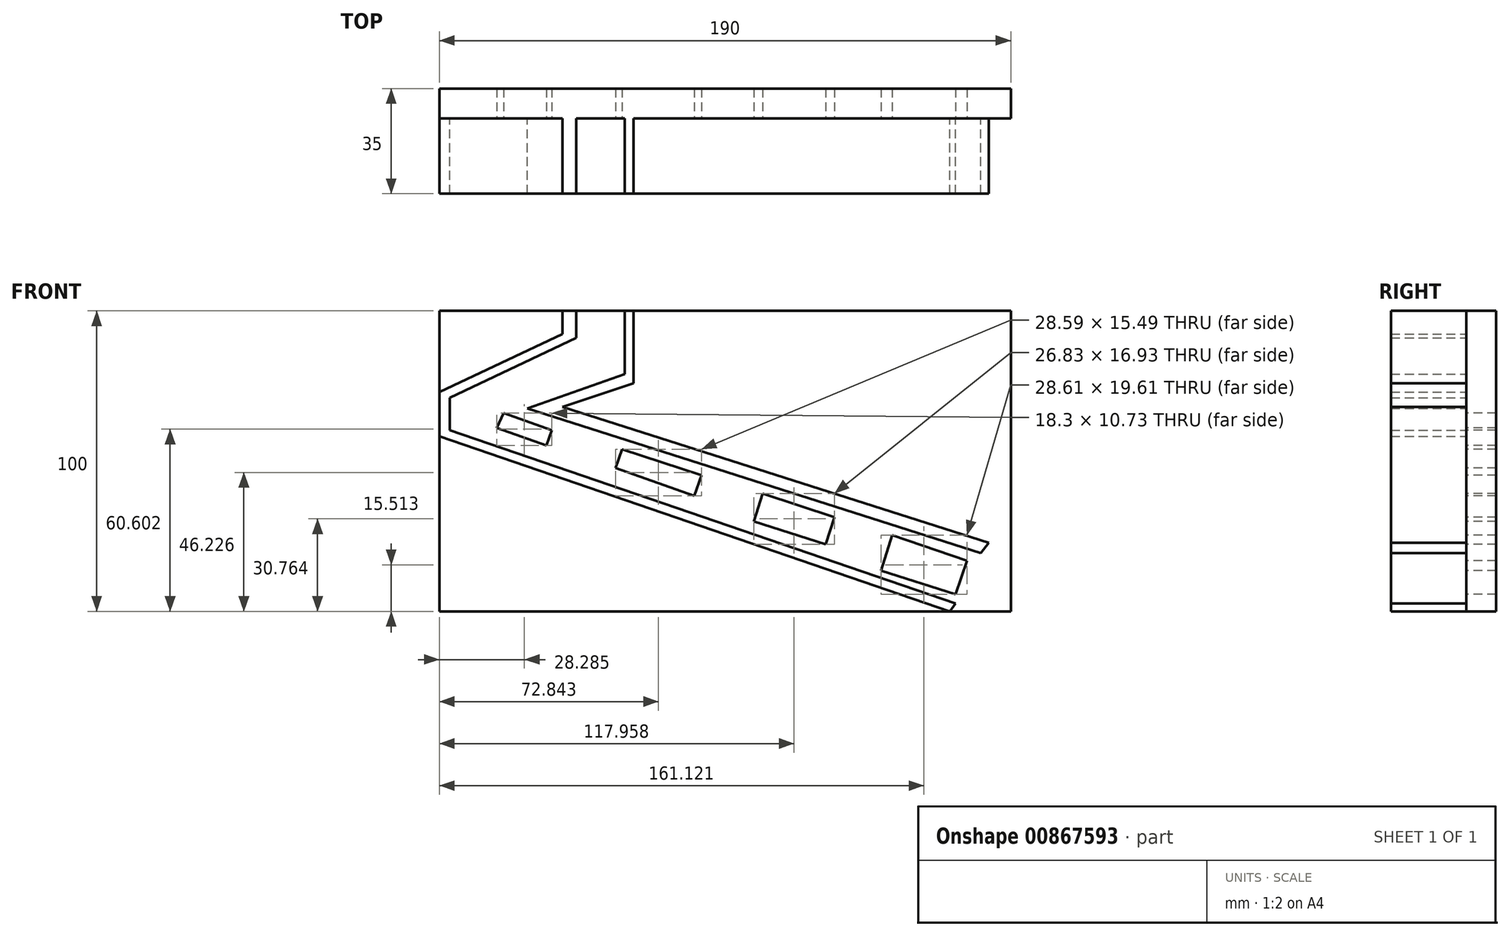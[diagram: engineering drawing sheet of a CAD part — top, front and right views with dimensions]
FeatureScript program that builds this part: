
annotation { "Feature Type Name" : "Feature", "Feature Type Description" : "" }
export const myFeature = defineFeature(function(context is Context, id is Id, definition is map)
    precondition{}
    {
        {
            var Q0;
            Q0=qCreatedBy(makeId("Front.planeOp"),FACE);
            var sketch = newSketch(context, id + "F0", { "sketchPlane" : qUnion([Q0])});
            skLineSegment(sketch, "E0.bottom", {"start": v(-95, 50) * mm, "end": v(95, 50) * mm});
            skLineSegment(sketch, "E0.top", {"start": v(-95, -50) * mm, "end": v(95, -50) * mm});
            skLineSegment(sketch, "E0.left", {"start": v(-95, 50) * mm, "end": v(-95, -50) * mm});
            skLineSegment(sketch, "E0.right", {"start": v(95, 50) * mm, "end": v(95, -50) * mm});
            skPoint(sketch, "E0.middle", {"position": v(0, 0) * mm});
            skSolve(sketch);
        }
        {
            var Q0;
            Q0 = qSketchRegion(id + "F0", true);
            extrude(context, id + "F1", {"entities" : qUnion([Q0]), "depth" : 10 * mm, "offsetDistance" : 25 * mm});
        }
        {
            var Q0;
            Q0=makeQuery(id+"F1.opExtrude","CAP_FACE",FACE,{"disambiguationData":[OSD([sQuery(id+"F0.wireOp",EDGE,"E0.bottom"),sQuery(id+"F0.wireOp",EDGE,"E0.top"),sQuery(id+"F0.wireOp",EDGE,"E0.left"),sQuery(id+"F0.wireOp",EDGE,"E0.right")])],"isStart":false});
            var sketch = newSketch(context, id + "F2", { "sketchPlane" : qUnion([Q0])});
            skLineSegment(sketch, "E1", {"start": v(-49.5, 50) * mm, "end": v(-49.5, 40.97) * mm});
            skLineSegment(sketch, "E2", {"start": v(-95, 8.3) * mm, "end": v(74.74, -50) * mm});
            skLineSegment(sketch, "E3", {"start": v(-33.3, 50) * mm, "end": v(-33.3, 40.97) * mm});
            skLineSegment(sketch, "E4", {"start": v(-33.3, 40.97) * mm, "end": v(-33.3, 28.9) * mm});
            skLineSegment(sketch, "E5", {"start": v(-33.3, 28.9) * mm, "end": v(-61.64, 18.92) * mm});
            skLineSegment(sketch, "E6", {"start": v(-61.64, 18.92) * mm, "end": v(-65.7, 17.5) * mm});
            skLineSegment(sketch, "E7", {"start": v(-65.7, 17.5) * mm, "end": v(85.05, -30.57) * mm});
            skLineSegment(sketch, "E8", {"start": v(-54.1, 50) * mm, "end": v(-54.1, 42.27) * mm});
            skLineSegment(sketch, "E9", {"start": v(-49.5, 40.97) * mm, "end": v(-88.56, 22.47) * mm});
            skLineSegment(sketch, "E10", {"start": v(-54.1, 42.27) * mm, "end": v(-95, 22.96) * mm});
            skLineSegment(sketch, "E11", {"start": v(-95, 22.96) * mm, "end": v(-95, 8.3) * mm});
            skLineSegment(sketch, "E12", {"start": v(-88.56, 22.47) * mm, "end": v(-91.55, 21.05) * mm});
            skLineSegment(sketch, "E13", {"start": v(-91.55, 21.05) * mm, "end": v(-91.55, 10.34) * mm});
            skLineSegment(sketch, "E14", {"start": v(-91.55, 10.34) * mm, "end": v(76.6, -47.4) * mm});
            skLineSegment(sketch, "E15", {"start": v(76.6, -47.4) * mm, "end": v(74.74, -50) * mm});
            skLineSegment(sketch, "E16", {"start": v(-49.5, 50) * mm, "end": v(-54.1, 50) * mm});
            skLineSegment(sketch, "E17", {"start": v(-30.39, 50) * mm, "end": v(-30.39, 25.93) * mm});
            skLineSegment(sketch, "E18", {"start": v(-30.39, 25.93) * mm, "end": v(-54.1, 18.01) * mm});
            skLineSegment(sketch, "E19", {"start": v(-54.1, 18.01) * mm, "end": v(87.65, -27.18) * mm});
            skLineSegment(sketch, "E20", {"start": v(87.65, -27.18) * mm, "end": v(85.05, -30.57) * mm});
            skLineSegment(sketch, "E21", {"start": v(-30.39, 50) * mm, "end": v(-33.3, 50) * mm});
            skLineSegment(sketch, "E22", {"start": v(-73.66, 15.97) * mm, "end": v(-57.57, 10.27) * mm});
            skLineSegment(sketch, "E23", {"start": v(-57.57, 10.27) * mm, "end": v(-59.35, 5.24) * mm});
            skLineSegment(sketch, "E24", {"start": v(-59.35, 5.24) * mm, "end": v(-75.86, 11.08) * mm});
            skLineSegment(sketch, "E25", {"start": v(-75.86, 11.08) * mm, "end": v(-73.66, 15.97) * mm});
            skLineSegment(sketch, "E26", {"start": v(-34.25, 3.97) * mm, "end": v(-36.45, -2.26) * mm});
            skLineSegment(sketch, "E27", {"start": v(-36.45, -2.26) * mm, "end": v(-10.29, -11.52) * mm});
            skLineSegment(sketch, "E28", {"start": v(-10.29, -11.52) * mm, "end": v(-7.86, -4.66) * mm});
            skLineSegment(sketch, "E29", {"start": v(-7.86, -4.66) * mm, "end": v(-34.25, 3.97) * mm});
            skLineSegment(sketch, "E30", {"start": v(12.5, -10.77) * mm, "end": v(9.54, -20.06) * mm});
            skLineSegment(sketch, "E31", {"start": v(9.54, -20.06) * mm, "end": v(33.51, -27.7) * mm});
            skLineSegment(sketch, "E32", {"start": v(33.51, -27.7) * mm, "end": v(36.37, -18.72) * mm});
            skLineSegment(sketch, "E33", {"start": v(36.37, -18.72) * mm, "end": v(12.5, -10.77) * mm});
            skLineSegment(sketch, "E34", {"start": v(55.55, -24.68) * mm, "end": v(51.82, -36.39) * mm});
            skLineSegment(sketch, "E35", {"start": v(51.82, -36.39) * mm, "end": v(76.6, -44.3) * mm});
            skLineSegment(sketch, "E36", {"start": v(76.6, -44.3) * mm, "end": v(80.42, -33.16) * mm});
            skLineSegment(sketch, "E37", {"start": v(80.42, -33.16) * mm, "end": v(55.55, -24.68) * mm});
            skSolve(sketch);
        }
        {
            var Q0;
            Q0=makeQuery(id+"F2.imprint","IMPRINT",FACE,{"disambiguationData":[TD([[makeQuery(id+"F2.imprint","IMPRINT",EDGE,{"derivedFrom":sQuery(id+"F2.wireOp",EDGE,"E1")}),-1.0]])]});
            var Q1;
            Q1=makeQuery(id+"F2.imprint","IMPRINT",FACE,{"disambiguationData":[TD([[makeQuery(id+"F2.imprint","IMPRINT",EDGE,{"derivedFrom":sQuery(id+"F2.wireOp",EDGE,"E3")}),1.0]])]});
            extrude(context, id + "F3", {"entities" : qUnion([Q0, Q1]), "operationType" : NewBodyOperationType.ADD, "depth" : 25 * mm, "offsetDistance" : 25 * mm});
        }
        {
            var Q0;
            Q0=makeQuery(id+"F2.imprint","IMPRINT",FACE,{"disambiguationData":[TD([[makeQuery(id+"F2.imprint","IMPRINT",EDGE,{"derivedFrom":sQuery(id+"F2.wireOp",EDGE,"E22")}),-1.0]])]});
            var Q1;
            Q1=makeQuery(id+"F2.imprint","IMPRINT",FACE,{"disambiguationData":[TD([[makeQuery(id+"F2.imprint","IMPRINT",EDGE,{"derivedFrom":sQuery(id+"F2.wireOp",EDGE,"E26")}),1.0]])]});
            var Q2;
            Q2=makeQuery(id+"F2.imprint","IMPRINT",FACE,{"disambiguationData":[TD([[makeQuery(id+"F2.imprint","IMPRINT",EDGE,{"derivedFrom":sQuery(id+"F2.wireOp",EDGE,"E30")}),1.0]])]});
            var Q3;
            Q3=makeQuery(id+"F2.imprint","IMPRINT",FACE,{"disambiguationData":[TD([[makeQuery(id+"F2.imprint","IMPRINT",EDGE,{"derivedFrom":sQuery(id+"F2.wireOp",EDGE,"E34")}),1.0]])]});
            extrude(context, id + "F4", {"entities" : qUnion([Q0, Q1, Q2, Q3]), "operationType" : NewBodyOperationType.REMOVE, "oppositeDirection" : true, "depth" : 25 * mm, "offsetDistance" : 25 * mm});
        }
    });
